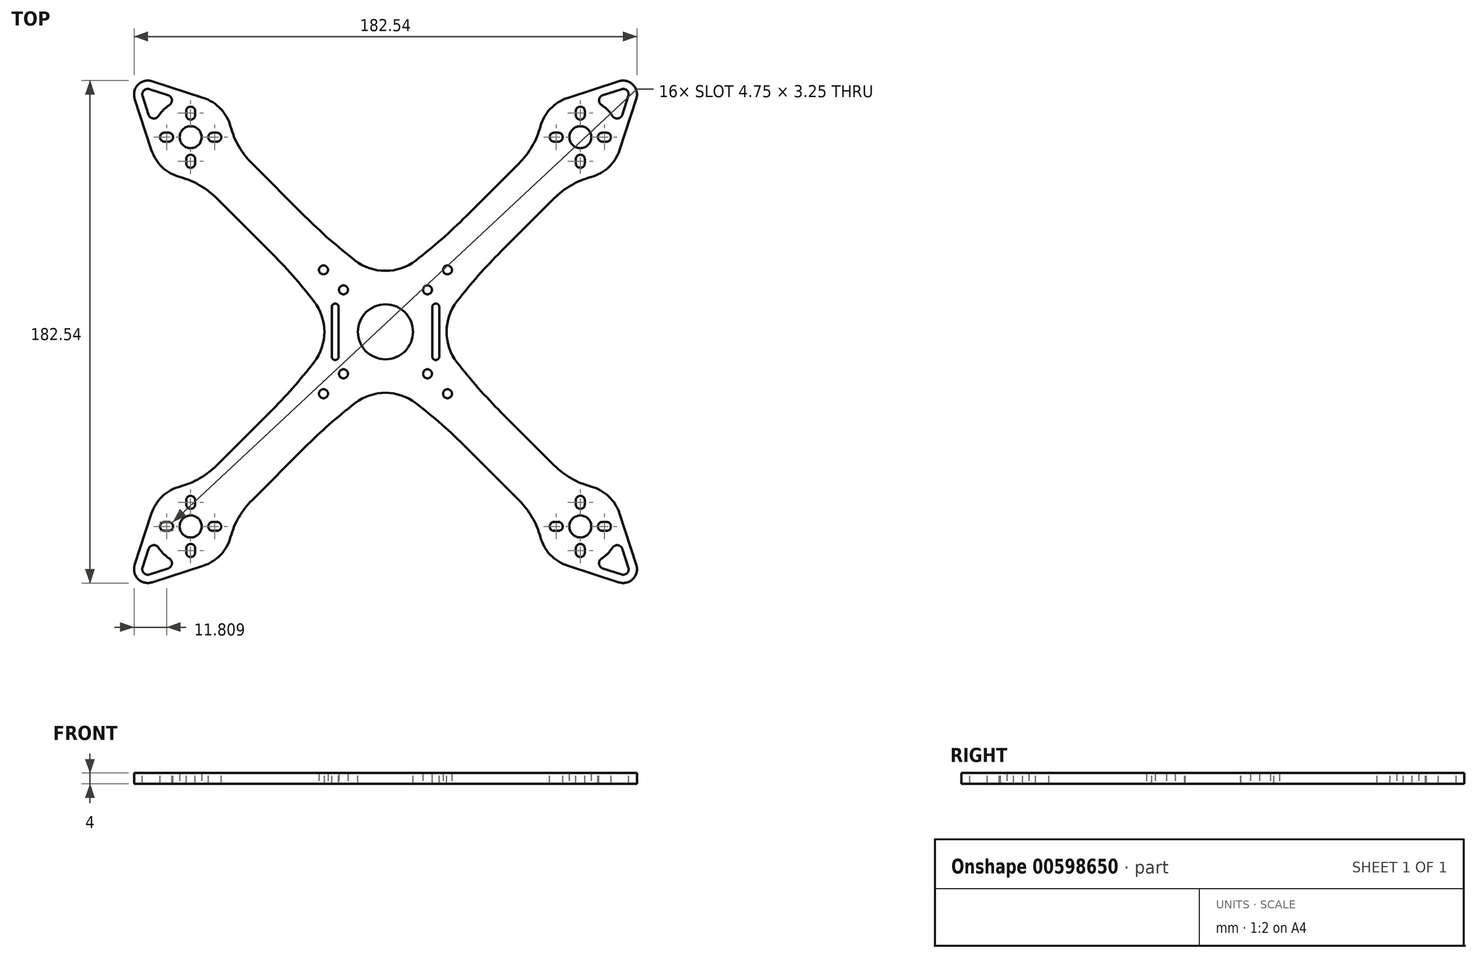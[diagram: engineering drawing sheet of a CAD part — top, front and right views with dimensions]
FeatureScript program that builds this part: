
annotation { "Feature Type Name" : "Feature", "Feature Type Description" : "" }
export const myFeature = defineFeature(function(context is Context, id is Id, definition is map)
    precondition{}
    {
        {
            var Q0;
            Q0=qCreatedBy(makeId("Top.planeOp"),FACE);
            var sketch = newSketch(context, id + "F0", { "sketchPlane" : qUnion([Q0])});
            skLineSegment(sketch, "E0", {"start": v(0, 0) * mm, "end": v(-70.71, 70.71) * mm, "construction": true});
            skCircle(sketch, "E1", {"center": v(-15.25, 15.25) * mm, "radius": 1.63 * mm});
            skLineSegment(sketch, "E2.bottom", {"start": v(-18, 18) * mm, "end": v(18, 18) * mm, "construction": true});
            skLineSegment(sketch, "E2.top", {"start": v(-18, -18) * mm, "end": v(18, -18) * mm, "construction": true});
            skLineSegment(sketch, "E2.left", {"start": v(-18, 18) * mm, "end": v(-18, -18) * mm, "construction": true});
            skLineSegment(sketch, "E2.right", {"start": v(18, 18) * mm, "end": v(18, -18) * mm, "construction": true});
            skPoint(sketch, "E2.middle", {"position": v(0, 0) * mm});
            skCircle(sketch, "E3", {"center": v(-70.71, 70.71) * mm, "radius": 4 * mm});
            skLineSegment(sketch, "E4", {"start": v(-70.71, 70.71) * mm, "end": v(-86.27, 86.27) * mm, "construction": true});
            skArc(sketch, "E5", {"start": v(-84.72, 91.02) * mm, "mid": v(-89.8, 89.8) * mm, "end": v(-91.02, 84.72) * mm});
            skLineSegment(sketch, "E6", {"start": v(-91.02, 84.72) * mm, "end": v(-84.98, 66.08) * mm});
            skLineSegment(sketch, "E7", {"start": v(-84.72, 91.02) * mm, "end": v(-66.08, 84.98) * mm});
            skArc(sketch, "E8.trimOffspring", {"start": v(-84.98, 66.08) * mm, "mid": v(-81.05, 59.84) * mm, "end": v(-74.61, 56.23) * mm});
            skLineSegment(sketch, "E9", {"start": v(-18, 0) * mm, "end": v(0, 0) * mm});
            skLineSegment(sketch, "E10", {"start": v(0, 0) * mm, "end": v(0, 18) * mm});
            skArc(sketch, "E11", {"start": v(-18, 0) * mm, "mid": v(-29.3, 15.25) * mm, "end": v(-42.03, 29.3) * mm});
            skArc(sketch, "E12.MirrorCS", {"start": v(0, 18) * mm, "mid": v(-15.25, 29.3) * mm, "end": v(-29.3, 42.03) * mm});
            skCircle(sketch, "E13", {"center": v(-70.71, 70.71) * mm, "radius": 64 * mm, "construction": true});
            skCircle(sketch, "E14", {"center": v(-22.5, 22.5) * mm, "radius": 1.63 * mm});
            skLineSegment(sketch, "E15", {"start": v(-42.03, 29.3) * mm, "end": v(-61.2, 48.47) * mm});
            skLineSegment(sketch, "E16.MirrorCS", {"start": v(-29.3, 42.03) * mm, "end": v(-48.47, 61.2) * mm});
            skArc(sketch, "E17.MirrorCS", {"start": v(-66.08, 84.98) * mm, "mid": v(-59.84, 81.05) * mm, "end": v(-56.23, 74.61) * mm});
            skPoint(sketch, "E18.visualSharp", {"position": v(-68.59, 55.86) * mm});
            skArc(sketch, "E18.filletArc", {"start": v(-61.2, 48.47) * mm, "mid": v(-67.4, 53.23) * mm, "end": v(-74.61, 56.23) * mm});
            skPoint(sketch, "E19.visualSharp", {"position": v(-55.86, 68.59) * mm});
            skArc(sketch, "E19.filletArc", {"start": v(-56.23, 74.61) * mm, "mid": v(-53.23, 67.4) * mm, "end": v(-48.47, 61.2) * mm});
            skSolve(sketch);
        }
        {
            var Q0;
            Q0=makeQuery(id+"F0.imprint","IMPRINT",FACE,{"disambiguationData":[TD([[makeQuery(id+"F0.imprint","IMPRINT",EDGE,{"derivedFrom":sQuery(id+"F0.wireOp",EDGE,"E1")}),-1.0]])]});
            extrude(context, id + "F1", {"entities" : qUnion([Q0]), "depth" : 4 * mm, "offsetDistance" : 25 * mm});
        }
        {
            var Q0;
            Q0=makeQuery(id+"F1.opExtrude","CAP_FACE",FACE,{"disambiguationData":[OSD([sQuery(id+"F0.wireOp",EDGE,"spTRh5jY-0KzT-nTe9-YrOm-80Ub0D9NBMuS"),sQuery(id+"F0.wireOp",EDGE,"Ztn7GRjr-ASCC-SAN5-Uun1-zx7WtjweK0g6"),sQuery(id+"F0.wireOp",EDGE,"0YCsi0T8-5uul-1h6W-62kf-haNI1vx5Sxbh"),sQuery(id+"F0.wireOp",EDGE,"E1"),sQuery(id+"F0.wireOp",EDGE,"3BKJBPn8-ic94-wUaa-LHyR-0beOCbis7ypq"),sQuery(id+"F0.wireOp",EDGE,"531242ed-003c-4ef5-ae37-b3655ad117b90.MirrorCS"),sQuery(id+"F0.wireOp",EDGE,"E3"),sQuery(id+"F0.wireOp",EDGE,"2c6f46fa-4c3f-4223-947a-6d7d458014a7.filletArc"),sQuery(id+"F0.wireOp",EDGE,"61032bae-fc5b-4c0e-833f-f82e544a5e7c.filletArc"),sQuery(id+"F0.wireOp",EDGE,"E5"),sQuery(id+"F0.wireOp",EDGE,"E6"),sQuery(id+"F0.wireOp",EDGE,"E7"),sQuery(id+"F0.wireOp",EDGE,"E8.trimOffspring"),sQuery(id+"F0.wireOp",EDGE,"E9"),sQuery(id+"F0.wireOp",EDGE,"E10")])],"isStart":false});
            var sketch = newSketch(context, id + "F2", { "sketchPlane" : qUnion([Q0])});
            skCircle(sketch, "E20", {"center": v(-70.71, 70.71) * mm, "radius": 8 * mm, "construction": true});
            skCircle(sketch, "E21", {"center": v(-70.71, 70.71) * mm, "radius": 9.5 * mm, "construction": true});
            skLineSegment(sketch, "E22", {"start": v(-70.71, 78.71) * mm, "end": v(-70.71, 80.21) * mm, "construction": true});
            skLineSegment(sketch, "E23", {"start": v(-70.71, 70.71) * mm, "end": v(-70.71, 78.71) * mm, "construction": true});
            skArc(sketch, "E24.0.startCap", {"start": v(-69.09, 78.71) * mm, "mid": v(-70.71, 77.09) * mm, "end": v(-72.34, 78.71) * mm});
            skArc(sketch, "E24.0.endCap", {"start": v(-72.34, 80.21) * mm, "mid": v(-70.71, 81.84) * mm, "end": v(-69.09, 80.21) * mm});
            skLineSegment(sketch, "E24.0.left", {"start": v(-72.34, 78.71) * mm, "end": v(-72.34, 80.21) * mm});
            skLineSegment(sketch, "E24.0.right", {"start": v(-69.09, 78.71) * mm, "end": v(-69.09, 80.21) * mm});
            skArc(sketch, "E25.1.0", {"start": v(-80.21, 69.09) * mm, "mid": v(-81.84, 70.71) * mm, "end": v(-80.21, 72.34) * mm});
            skArc(sketch, "E25.1.1", {"start": v(-78.71, 72.34) * mm, "mid": v(-77.09, 70.71) * mm, "end": v(-78.71, 69.09) * mm});
            skLineSegment(sketch, "E25.1.2", {"start": v(-78.71, 69.09) * mm, "end": v(-80.21, 69.09) * mm});
            skLineSegment(sketch, "E25.1.3", {"start": v(-78.71, 70.71) * mm, "end": v(-80.21, 70.71) * mm, "construction": true});
            skLineSegment(sketch, "E25.1.4", {"start": v(-78.71, 72.34) * mm, "end": v(-80.21, 72.34) * mm});
            skArc(sketch, "E25.2.0", {"start": v(-69.09, 61.21) * mm, "mid": v(-70.71, 59.59) * mm, "end": v(-72.34, 61.21) * mm});
            skArc(sketch, "E25.2.1", {"start": v(-72.34, 62.71) * mm, "mid": v(-70.71, 64.34) * mm, "end": v(-69.09, 62.71) * mm});
            skLineSegment(sketch, "E25.2.2", {"start": v(-69.09, 62.71) * mm, "end": v(-69.09, 61.21) * mm});
            skLineSegment(sketch, "E25.2.3", {"start": v(-70.71, 62.71) * mm, "end": v(-70.71, 61.21) * mm, "construction": true});
            skLineSegment(sketch, "E25.2.4", {"start": v(-72.34, 62.71) * mm, "end": v(-72.34, 61.21) * mm});
            skArc(sketch, "E25.3.0", {"start": v(-61.21, 72.34) * mm, "mid": v(-59.59, 70.71) * mm, "end": v(-61.21, 69.09) * mm});
            skArc(sketch, "E25.3.1", {"start": v(-62.71, 69.09) * mm, "mid": v(-64.34, 70.71) * mm, "end": v(-62.71, 72.34) * mm});
            skLineSegment(sketch, "E25.3.2", {"start": v(-62.71, 72.34) * mm, "end": v(-61.21, 72.34) * mm});
            skLineSegment(sketch, "E25.3.3", {"start": v(-62.71, 70.71) * mm, "end": v(-61.21, 70.71) * mm, "construction": true});
            skLineSegment(sketch, "E25.3.4", {"start": v(-62.71, 69.09) * mm, "end": v(-61.21, 69.09) * mm});
            skLineSegment(sketch, "E26", {"start": v(-70.71, 70.71) * mm, "end": v(-62.71, 70.71) * mm, "construction": true});
            skSolve(sketch);
        }
        {
            var Q0;
            Q0 = qSketchRegion(id + "F2", true);
            extrude(context, id + "F3", {"entities" : qUnion([Q0]), "operationType" : NewBodyOperationType.REMOVE, "oppositeDirection" : true, "depth" : 25 * mm, "offsetDistance" : 25 * mm});
        }
        {
            var Q0;
            Q0=makeQuery(id+"F1.opExtrude","CAP_FACE",FACE,{"disambiguationData":[OSD([sQuery(id+"F0.wireOp",EDGE,"spTRh5jY-0KzT-nTe9-YrOm-80Ub0D9NBMuS"),sQuery(id+"F0.wireOp",EDGE,"Ztn7GRjr-ASCC-SAN5-Uun1-zx7WtjweK0g6"),sQuery(id+"F0.wireOp",EDGE,"0YCsi0T8-5uul-1h6W-62kf-haNI1vx5Sxbh"),sQuery(id+"F0.wireOp",EDGE,"E1"),sQuery(id+"F0.wireOp",EDGE,"3BKJBPn8-ic94-wUaa-LHyR-0beOCbis7ypq"),sQuery(id+"F0.wireOp",EDGE,"531242ed-003c-4ef5-ae37-b3655ad117b90.MirrorCS"),sQuery(id+"F0.wireOp",EDGE,"E3"),sQuery(id+"F0.wireOp",EDGE,"2c6f46fa-4c3f-4223-947a-6d7d458014a7.filletArc"),sQuery(id+"F0.wireOp",EDGE,"61032bae-fc5b-4c0e-833f-f82e544a5e7c.filletArc"),sQuery(id+"F0.wireOp",EDGE,"E5"),sQuery(id+"F0.wireOp",EDGE,"E6"),sQuery(id+"F0.wireOp",EDGE,"E7"),sQuery(id+"F0.wireOp",EDGE,"E8.trimOffspring"),sQuery(id+"F0.wireOp",EDGE,"E9"),sQuery(id+"F0.wireOp",EDGE,"E10")])],"isStart":false});
            var sketch = newSketch(context, id + "F4", { "sketchPlane" : qUnion([Q0])});
            skArc(sketch, "E27", {"start": v(-78.4, 82.4) * mm, "mid": v(-80.61, 80.61) * mm, "end": v(-82.4, 78.4) * mm});
            skArc(sketch, "E28", {"start": v(-85.65, 88.17) * mm, "mid": v(-87.68, 87.68) * mm, "end": v(-88.17, 85.65) * mm});
            skLineSegment(sketch, "E29", {"start": v(-85.65, 88.17) * mm, "end": v(-78.9, 85.98) * mm});
            skLineSegment(sketch, "E30", {"start": v(-88.17, 85.65) * mm, "end": v(-85.98, 78.9) * mm});
            skPoint(sketch, "E31.visualSharp", {"position": v(-84.35, 73.87) * mm});
            skArc(sketch, "E31.filletArc", {"start": v(-85.98, 78.9) * mm, "mid": v(-84.34, 77.53) * mm, "end": v(-82.4, 78.4) * mm});
            skPoint(sketch, "E32.visualSharp", {"position": v(-73.87, 84.35) * mm});
            skArc(sketch, "E32.filletArc", {"start": v(-78.4, 82.4) * mm, "mid": v(-77.53, 84.34) * mm, "end": v(-78.9, 85.98) * mm});
            skSolve(sketch);
        }
        {
            var Q0;
            Q0=makeQuery(id+"F4.imprint","IMPRINT",FACE,{"disambiguationData":[TD([[makeQuery(id+"F4.imprint","IMPRINT",EDGE,{"derivedFrom":sQuery(id+"F4.wireOp",EDGE,"E27")}),-1.0]])]});
            extrude(context, id + "F5", {"entities" : qUnion([Q0]), "operationType" : NewBodyOperationType.REMOVE, "oppositeDirection" : true, "depth" : 25 * mm, "offsetDistance" : 25 * mm});
        }
        {
            var Q0;
            Q0=makeQuery(id+"F1.opExtrude","SWEPT_BODY",BODY,{"disambiguationData":[OSD([sQuery(id+"F0.wireOp",EDGE,"spTRh5jY-0KzT-nTe9-YrOm-80Ub0D9NBMuS"),sQuery(id+"F0.wireOp",EDGE,"Ztn7GRjr-ASCC-SAN5-Uun1-zx7WtjweK0g6"),sQuery(id+"F0.wireOp",EDGE,"0YCsi0T8-5uul-1h6W-62kf-haNI1vx5Sxbh"),sQuery(id+"F0.wireOp",EDGE,"E1"),sQuery(id+"F0.wireOp",EDGE,"3BKJBPn8-ic94-wUaa-LHyR-0beOCbis7ypq"),sQuery(id+"F0.wireOp",EDGE,"531242ed-003c-4ef5-ae37-b3655ad117b90.MirrorCS"),sQuery(id+"F0.wireOp",EDGE,"E3"),sQuery(id+"F0.wireOp",EDGE,"2c6f46fa-4c3f-4223-947a-6d7d458014a7.filletArc"),sQuery(id+"F0.wireOp",EDGE,"61032bae-fc5b-4c0e-833f-f82e544a5e7c.filletArc"),sQuery(id+"F0.wireOp",EDGE,"E5"),sQuery(id+"F0.wireOp",EDGE,"E6"),sQuery(id+"F0.wireOp",EDGE,"E7"),sQuery(id+"F0.wireOp",EDGE,"E8.trimOffspring"),sQuery(id+"F0.wireOp",EDGE,"E9"),sQuery(id+"F0.wireOp",EDGE,"E10")])]});
            var Q1;
            Q1=makeQuery(id+"F1.opExtrude","SWEPT_EDGE",EDGE,{"disambiguationData":[OSD([sQuery(id+"F0.wireOp",EDGE,"E9"),sQuery(id+"F0.wireOp",EDGE,"E10")])]});
            circularPattern(context, id + "F6", {"operationType" : NewBodyOperationType.ADD, "entities" : qUnion([Q0]), "axis" : qUnion([Q1]), "angle" : 360 * degree, "instanceCount" : 4, "equalSpace" : true});
        }
        {
            var Q0;
            Q0=makeQuery(id+"F6.boolean.opBoolean","MERGE",EDGE,{"derivedFrom":[makeQuery(id+"F1.opExtrude","SWEPT_EDGE",EDGE,{"disambiguationData":[OSD([sQuery(id+"F0.wireOp",EDGE,"E9"),sQuery(id+"F0.wireOp",EDGE,"E11")])]}),makeQuery(id+"F6.opPattern","COPY",EDGE,{"derivedFrom":makeQuery(id+"F1.opExtrude","SWEPT_EDGE",EDGE,{"disambiguationData":[OSD([sQuery(id+"F0.wireOp",EDGE,"E10"),sQuery(id+"F0.wireOp",EDGE,"E12.MirrorCS")])]}),"instanceName":"3"})]});
            var Q1;
            Q1=makeQuery(id+"F6.boolean.opBoolean","MERGE",EDGE,{"derivedFrom":[makeQuery(id+"F1.opExtrude","SWEPT_EDGE",EDGE,{"disambiguationData":[OSD([sQuery(id+"F0.wireOp",EDGE,"E10"),sQuery(id+"F0.wireOp",EDGE,"E12.MirrorCS")])]}),makeQuery(id+"F6.opPattern","COPY",EDGE,{"derivedFrom":makeQuery(id+"F1.opExtrude","SWEPT_EDGE",EDGE,{"disambiguationData":[OSD([sQuery(id+"F0.wireOp",EDGE,"E9"),sQuery(id+"F0.wireOp",EDGE,"E11")])]}),"instanceName":"1"})]});
            var Q2;
            Q2=makeQuery(id+"F6.boolean.opBoolean","MERGE",EDGE,{"derivedFrom":[makeQuery(id+"F6.opPattern","COPY",EDGE,{"derivedFrom":makeQuery(id+"F1.opExtrude","SWEPT_EDGE",EDGE,{"disambiguationData":[OSD([sQuery(id+"F0.wireOp",EDGE,"E10"),sQuery(id+"F0.wireOp",EDGE,"E12.MirrorCS")])]}),"instanceName":"1"}),makeQuery(id+"F6.opPattern","COPY",EDGE,{"derivedFrom":makeQuery(id+"F1.opExtrude","SWEPT_EDGE",EDGE,{"disambiguationData":[OSD([sQuery(id+"F0.wireOp",EDGE,"E9"),sQuery(id+"F0.wireOp",EDGE,"E11")])]}),"instanceName":"2"})]});
            var Q3;
            Q3=makeQuery(id+"F6.boolean.opBoolean","MERGE",EDGE,{"derivedFrom":[makeQuery(id+"F6.opPattern","COPY",EDGE,{"derivedFrom":makeQuery(id+"F1.opExtrude","SWEPT_EDGE",EDGE,{"disambiguationData":[OSD([sQuery(id+"F0.wireOp",EDGE,"E10"),sQuery(id+"F0.wireOp",EDGE,"E12.MirrorCS")])]}),"instanceName":"2"}),makeQuery(id+"F6.opPattern","COPY",EDGE,{"derivedFrom":makeQuery(id+"F1.opExtrude","SWEPT_EDGE",EDGE,{"disambiguationData":[OSD([sQuery(id+"F0.wireOp",EDGE,"E9"),sQuery(id+"F0.wireOp",EDGE,"E11")])]}),"instanceName":"3"})]});
            fillet(context, id + "F7", {"entities" : qUnion([Q0, Q1, Q2, Q3]), "radius" : 18 * mm, "tangentPropagation" : true, "allowEdgeOverflow" : false});
        }
        {
            var Q0;
            {var subQ0=makeQuery(id+"F1.opExtrude","CAP_FACE",FACE,{"disambiguationData":[OSD([sQuery(id+"F0.wireOp",EDGE,"spTRh5jY-0KzT-nTe9-YrOm-80Ub0D9NBMuS"),sQuery(id+"F0.wireOp",EDGE,"Ztn7GRjr-ASCC-SAN5-Uun1-zx7WtjweK0g6"),sQuery(id+"F0.wireOp",EDGE,"0YCsi0T8-5uul-1h6W-62kf-haNI1vx5Sxbh"),sQuery(id+"F0.wireOp",EDGE,"E1"),sQuery(id+"F0.wireOp",EDGE,"3BKJBPn8-ic94-wUaa-LHyR-0beOCbis7ypq"),sQuery(id+"F0.wireOp",EDGE,"531242ed-003c-4ef5-ae37-b3655ad117b90.MirrorCS"),sQuery(id+"F0.wireOp",EDGE,"E3"),sQuery(id+"F0.wireOp",EDGE,"2c6f46fa-4c3f-4223-947a-6d7d458014a7.filletArc"),sQuery(id+"F0.wireOp",EDGE,"61032bae-fc5b-4c0e-833f-f82e544a5e7c.filletArc"),sQuery(id+"F0.wireOp",EDGE,"E5"),sQuery(id+"F0.wireOp",EDGE,"E6"),sQuery(id+"F0.wireOp",EDGE,"E7"),sQuery(id+"F0.wireOp",EDGE,"E8.trimOffspring"),sQuery(id+"F0.wireOp",EDGE,"E9"),sQuery(id+"F0.wireOp",EDGE,"E10")])],"isStart":false});Q0=makeQuery(id+"F6.boolean.opBoolean","MERGE",FACE,{"derivedFrom":[subQ0,makeQuery(id+"F6.opPattern","COPY",FACE,{"derivedFrom":subQ0,"instanceName":"1"}),makeQuery(id+"F6.opPattern","COPY",FACE,{"derivedFrom":subQ0,"instanceName":"2"}),makeQuery(id+"F6.opPattern","COPY",FACE,{"derivedFrom":subQ0,"instanceName":"3"})]});}
            var sketch = newSketch(context, id + "F8", { "sketchPlane" : qUnion([Q0])});
            skLineSegment(sketch, "E33", {"start": v(-18.25, 9) * mm, "end": v(-18.25, -9) * mm, "construction": true});
            skArc(sketch, "E34.0.startCap", {"start": v(-19.5, 9) * mm, "mid": v(-18.25, 10.25) * mm, "end": v(-17, 9) * mm});
            skArc(sketch, "E34.0.endCap", {"start": v(-17, -9) * mm, "mid": v(-18.25, -10.25) * mm, "end": v(-19.5, -9) * mm});
            skLineSegment(sketch, "E34.0.left", {"start": v(-17, 9) * mm, "end": v(-17, -9) * mm});
            skLineSegment(sketch, "E34.0.right", {"start": v(-19.5, 9) * mm, "end": v(-19.5, -9) * mm});
            skLineSegment(sketch, "E35.MirrorCS", {"start": v(18.25, 9) * mm, "end": v(18.25, -9) * mm, "construction": true});
            skArc(sketch, "E36.MirrorCS", {"start": v(19.5, 9) * mm, "mid": v(18.25, 10.25) * mm, "end": v(17, 9) * mm});
            skArc(sketch, "E37.MirrorCS", {"start": v(17, -9) * mm, "mid": v(18.25, -10.25) * mm, "end": v(19.5, -9) * mm});
            skLineSegment(sketch, "E38.MirrorCS", {"start": v(17, 9) * mm, "end": v(17, -9) * mm});
            skLineSegment(sketch, "E39.MirrorCS", {"start": v(19.5, 9) * mm, "end": v(19.5, -9) * mm});
            skSolve(sketch);
        }
        {
            var Q0;
            Q0 = qSketchRegion(id + "F8", true);
            extrude(context, id + "F9", {"entities" : qUnion([Q0]), "operationType" : NewBodyOperationType.REMOVE, "oppositeDirection" : true, "depth" : 25 * mm, "offsetDistance" : 25 * mm});
        }
        {
            var Q0;
            {var subQ0=makeQuery(id+"F1.opExtrude","CAP_FACE",FACE,{"disambiguationData":[OSD([sQuery(id+"F0.wireOp",EDGE,"spTRh5jY-0KzT-nTe9-YrOm-80Ub0D9NBMuS"),sQuery(id+"F0.wireOp",EDGE,"E1"),sQuery(id+"F0.wireOp",EDGE,"E3"),sQuery(id+"F0.wireOp",EDGE,"E5"),sQuery(id+"F0.wireOp",EDGE,"E6"),sQuery(id+"F0.wireOp",EDGE,"E7"),sQuery(id+"F0.wireOp",EDGE,"E8.trimOffspring"),sQuery(id+"F0.wireOp",EDGE,"E9"),sQuery(id+"F0.wireOp",EDGE,"E10"),sQuery(id+"F0.wireOp",EDGE,"E11"),sQuery(id+"F0.wireOp",EDGE,"E12.MirrorCS"),sQuery(id+"F0.wireOp",EDGE,"E14")])],"isStart":false});Q0=makeQuery(id+"F6.boolean.opBoolean","MERGE",FACE,{"derivedFrom":[subQ0,makeQuery(id+"F6.opPattern","COPY",FACE,{"derivedFrom":subQ0,"instanceName":"1"}),makeQuery(id+"F6.opPattern","COPY",FACE,{"derivedFrom":subQ0,"instanceName":"2"}),makeQuery(id+"F6.opPattern","COPY",FACE,{"derivedFrom":subQ0,"instanceName":"3"})]});}
            var sketch = newSketch(context, id + "F10", { "sketchPlane" : qUnion([Q0])});
            skCircle(sketch, "E40", {"center": v(0, 0) * mm, "radius": 10 * mm});
            skSolve(sketch);
        }
        {
            var Q0;
            Q0=makeQuery(id+"F10.imprint","IMPRINT",FACE,{"disambiguationData":[TD([[makeQuery(id+"F10.imprint","IMPRINT",EDGE,{"derivedFrom":sQuery(id+"F10.wireOp",EDGE,"E40")}),1.0]])]});
            extrude(context, id + "F11", {"entities" : qUnion([Q0]), "operationType" : NewBodyOperationType.REMOVE, "oppositeDirection" : true, "depth" : 25 * mm, "offsetDistance" : 25 * mm});
        }
    });
